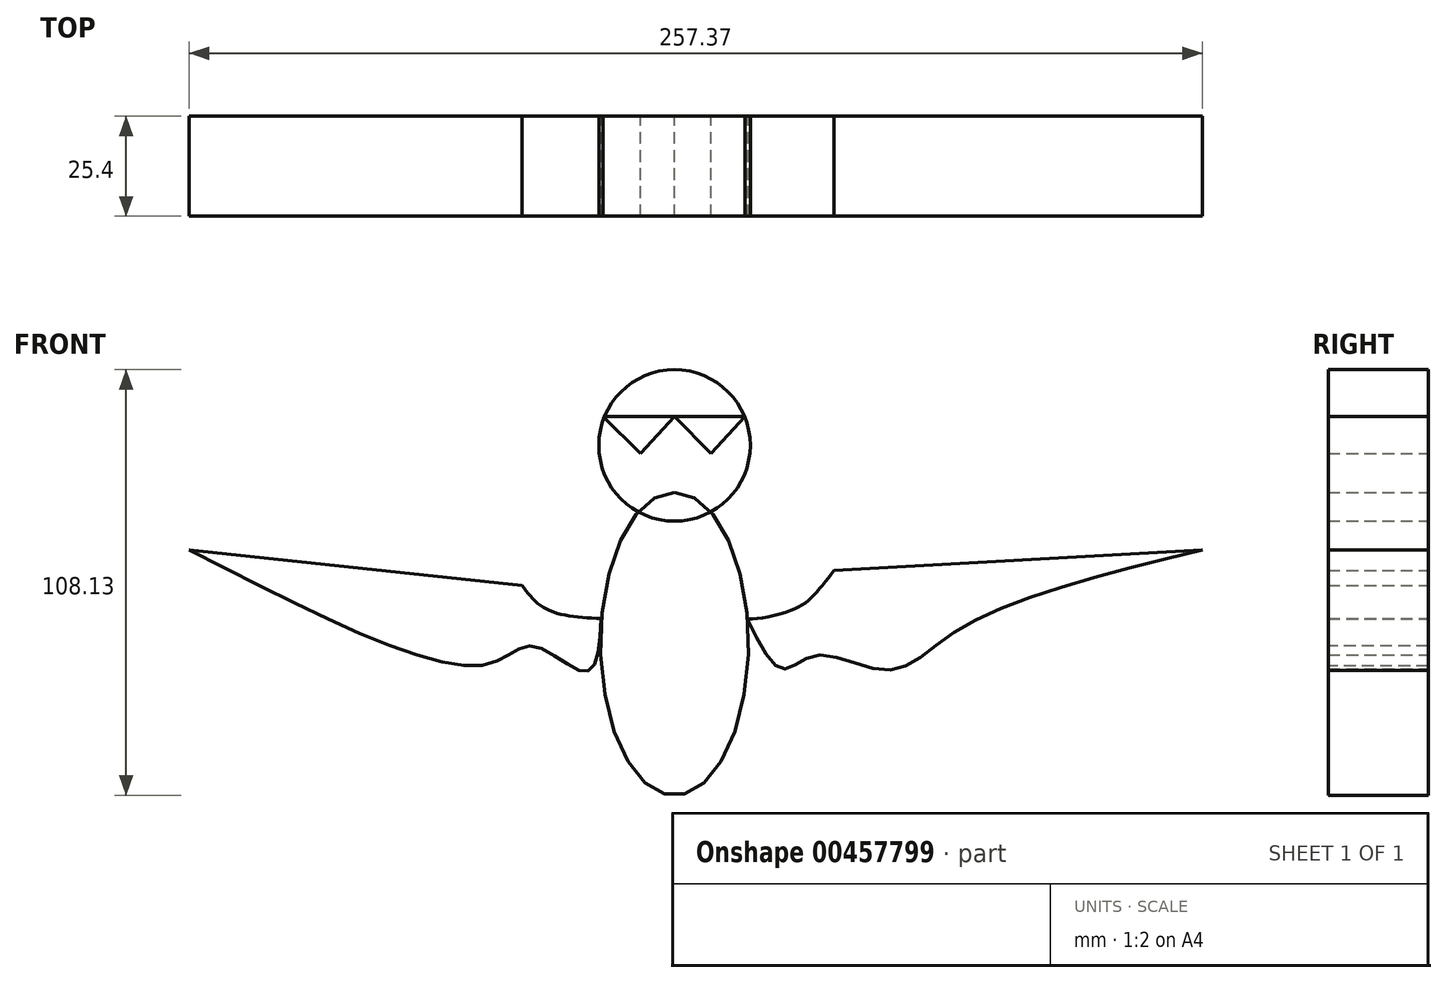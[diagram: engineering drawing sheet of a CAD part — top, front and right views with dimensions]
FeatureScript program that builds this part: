
annotation { "Feature Type Name" : "Feature", "Feature Type Description" : "" }
export const myFeature = defineFeature(function(context is Context, id is Id, definition is map)
    precondition{}
    {
        {
            var Q0;
            Q0=qCreatedBy(makeId("Front.planeOp"),FACE);
            var sketch = newSketch(context, id + "F0", { "sketchPlane" : qUnion([Q0])});
            skEllipse(sketch, "E0", {"center": v(0, -3.64) * mm, "majorRadius": 38.47 * mm, "minorRadius": 18.8 * mm, "majorAxis": v(0, 1)});
            skSolve(sketch);
        }
        {
            var Q0;
            Q0=qCreatedBy(makeId("Front.planeOp"),FACE);
            var sketch = newSketch(context, id + "F1", { "sketchPlane" : qUnion([Q0])});
            skFitSpline(sketch, "E1", {"points": [v(18.07, 8.3) * mm, v(25.36, 9.47) * mm, v(29.73, 20.26) * mm, v(31.48, 21.13) * mm, v(31.48, 20.55) * mm], "startDerivative": vector(25.4, -3.63) * mm, "endDerivative": vector(-2.02, -7.65) * mm});
            skLineSegment(sketch, "E2", {"start": v(31.54, 20.78) * mm, "end": v(134.08, 20.26) * mm});
            skLineSegment(sketch, "E3", {"start": v(134.08, 20.26) * mm, "end": v(40.52, 15.01) * mm});
            skFitSpline(sketch, "E4", {"points": [v(40.52, 15.01) * mm, v(34.98, 8.3) * mm, v(28.56, 4.52) * mm, v(18.36, 2.77) * mm, v(18.07, 3.35) * mm], "startDerivative": vector(-18.3, -24.2) * mm, "endDerivative": vector(-0.2, 8.2) * mm});
            skLineSegment(sketch, "E5", {"start": v(18.07, 8.3) * mm, "end": v(18.08, 3.12) * mm});
            skFitSpline(sketch, "E6", {"points": [v(18.36, 2.77) * mm, v(27.7, -10.06) * mm, v(35.85, -6.56) * mm, v(54.21, -10.35) * mm, v(72.29, 0) * mm, v(134.08, 20.26) * mm], "startDerivative": vector(55.94, -113.08) * mm, "endDerivative": vector(214.67, 52.98) * mm});
            skFitSpline(sketch, "E7", {"points": [v(-17.78, 8.3) * mm, v(-25.94, 8.3) * mm, v(-32.65, 19.67) * mm, v(-33.81, 20.26) * mm], "startDerivative": vector(-23.11, -7.76) * mm, "endDerivative": vector(-7.24, 0.33) * mm});
            skLineSegment(sketch, "E8", {"start": v(-33.81, 20.26) * mm, "end": v(-123.3, 20.26) * mm});
            skLineSegment(sketch, "E9", {"start": v(-123.3, 20.26) * mm, "end": v(-38.77, 11.22) * mm});
            skFitSpline(sketch, "E10", {"points": [v(-38.77, 11.22) * mm, v(-32.35, 5.1) * mm, v(-18.65, 2.77) * mm], "startDerivative": vector(12.18, -15.91) * mm, "endDerivative": vector(27.48, -1.53) * mm});
            skFitSpline(sketch, "E11", {"points": [v(-18.65, 2.77) * mm, v(-22.44, -10.64) * mm, v(-35.85, -4.23) * mm, v(-47.8, -8.9) * mm, v(-123.3, 20.26) * mm], "startDerivative": vector(-6.13, -105.57) * mm, "endDerivative": vector(-208.55, 107.64) * mm});
            skSolve(sketch);
        }
        {
            var Q0;
            Q0=qCreatedBy(makeId("Front.planeOp"),FACE);
            var sketch = newSketch(context, id + "F2", { "sketchPlane" : qUnion([Q0])});
            skFitSpline(sketch, "E12", {"points": [v(-10.1, -36.7) * mm, v(-24.14, -47.71) * mm, v(-22.71, -51.45) * mm, v(-17.74, -50.2) * mm, v(-22.36, -56.6) * mm, v(-20.76, -59.27) * mm, v(-11.16, -52.51) * mm, v(-6.36, -62.3) * mm, v(-4.05, -59.45) * mm, v(-8.31, -48.42) * mm, v(-5.3, -40.07) * mm], "startDerivative": vector(-127.16, -73.02) * mm, "endDerivative": vector(50.63, 74.74) * mm});
            skFitSpline(sketch, "E13", {"points": [v(9.11, -37.22) * mm, v(8.22, -43.98) * mm, v(8.93, -59.63) * mm, v(13.56, -59.98) * mm, v(13.56, -55.18) * mm, v(26.53, -59.63) * mm, v(27.25, -54.65) * mm, v(22.45, -54.3) * mm, v(25.82, -49.31) * mm, v(21.56, -47.36) * mm, v(16.4, -44.7) * mm, v(11.24, -34.02) * mm], "startDerivative": vector(-7.34, -61.02) * mm, "endDerivative": vector(-40.78, 108.1) * mm});
            skSolve(sketch);
        }
        {
            var Q0;
            Q0=qCreatedBy(makeId("Front.planeOp"),FACE);
            var sketch = newSketch(context, id + "F3", { "sketchPlane" : qUnion([Q0])});
            skFitSpline(sketch, "E14", {"points": [v(-18.25, 8.13) * mm, v(-20.7, -29.1) * mm, v(-16.14, -23.13) * mm], "startDerivative": vector(-9.88, -79.23) * mm, "endDerivative": vector(17.58, 30.62) * mm});
            skFitSpline(sketch, "E15", {"points": [v(18.29, 8.49) * mm, v(21.8, -23.13) * mm, v(22.86, -29.8) * mm, v(16.18, -23.13) * mm], "startDerivative": vector(5.55, -71.26) * mm, "endDerivative": vector(-32.66, 38.12) * mm});
            skSolve(sketch);
        }
        {
            var Q0;
            Q0=qCreatedBy(makeId("Front.planeOp"),FACE);
            var sketch = newSketch(context, id + "F4", { "sketchPlane" : qUnion([Q0])});
            skCircle(sketch, "E16", {"center": v(0, 46.77) * mm, "radius": 19.24 * mm});
            skSolve(sketch);
        }
        {
            var Q0;
            Q0=qCreatedBy(makeId("Front.planeOp"),FACE);
            var sketch = newSketch(context, id + "F5", { "sketchPlane" : qUnion([Q0])});
            skLineSegment(sketch, "E17", {"start": v(-18.22, 54.07) * mm, "end": v(0, 54.07) * mm});
            skLineSegment(sketch, "E18", {"start": v(0, 54.07) * mm, "end": v(-8.6, 44.74) * mm});
            skLineSegment(sketch, "E19", {"start": v(-8.6, 44.74) * mm, "end": v(-18.22, 54.07) * mm});
            skLineSegment(sketch, "E20", {"start": v(0, 54.07) * mm, "end": v(17.93, 54.07) * mm});
            skLineSegment(sketch, "E21", {"start": v(17.93, 54.07) * mm, "end": v(9.33, 44.74) * mm});
            skLineSegment(sketch, "E22", {"start": v(9.33, 44.74) * mm, "end": v(0, 54.07) * mm});
            skLineSegment(sketch, "E23", {"start": v(-8.6, 37.45) * mm, "end": v(0, 29.53) * mm});
            skLineSegment(sketch, "E24", {"start": v(0, 29.53) * mm, "end": v(7.7, 37.46) * mm});
            skSolve(sketch);
        }
        {
            var Q0;
            Q0=makeQuery(id+"F0.imprint","IMPRINT",FACE,{"disambiguationData":[TD([[makeQuery(id+"F0.imprint","IMPRINT",EDGE,{"derivedFrom":sQuery(id+"F0.wireOp",EDGE,"E0")}),1.0]])]});
            var Q1;
            {var subQ0=sQuery(id+"F1.wireOp",EDGE,"E3");Q1=makeQuery(id+"F1.imprint","IMPRINT",FACE,{"disambiguationData":[TD([[makeQuery(id+"F1.imprint","IMPRINT",EDGE,{"derivedFrom":subQ0}),1.0]])]});}
            var Q2;
            Q2=makeQuery(id+"F1.imprint","IMPRINT",FACE,{"disambiguationData":[TD([[makeQuery(id+"F1.imprint","IMPRINT",EDGE,{"derivedFrom":sQuery(id+"F1.wireOp",EDGE,"E9")}),-1.0]])]});
            var Q3;
            Q3=makeQuery(id+"F4.imprint","IMPRINT",FACE,{"disambiguationData":[TD([[makeQuery(id+"F4.imprint","IMPRINT",EDGE,{"derivedFrom":sQuery(id+"F4.wireOp",EDGE,"E16")}),1.0]])]});
            var Q4;
            Q4=makeQuery(id+"F5.imprint","IMPRINT",FACE,{"disambiguationData":[TD([[makeQuery(id+"F5.imprint","IMPRINT",EDGE,{"derivedFrom":sQuery(id+"F5.wireOp",EDGE,"E17")}),-1.0]])]});
            var Q5;
            Q5=makeQuery(id+"F5.imprint","IMPRINT",FACE,{"disambiguationData":[TD([[makeQuery(id+"F5.imprint","IMPRINT",EDGE,{"derivedFrom":sQuery(id+"F5.wireOp",EDGE,"E20")}),-1.0]])]});
            extrude(context, id + "F6", {"entities" : qUnion([Q0, Q1, Q2, Q3, Q4, Q5]), "depth" : 25.4 * mm});
        }
        {
            var Q0;
            Q0=sQuery(id+"F3.wireOp",EDGE,"E14");
            extrude(context, id + "F7", {"bodyType" : ToolBodyType.SURFACE, "surfaceEntities" : qUnion([Q0]), "depth" : 25.4 * mm});
        }
        {
            var Q0;
            Q0=qCreatedBy(makeId("Front.planeOp"),FACE);
            var sketch = newSketch(context, id + "F8", { "sketchPlane" : qUnion([Q0])});
            skFitSpline(sketch, "E25", {"points": [v(18.5, 0) * mm, v(20.55, -29.3) * mm, v(16.18, -24.63) * mm], "startDerivative": vector(8.7, -62.6) * mm, "endDerivative": vector(-16.4, 23.82) * mm});
            skSolve(sketch);
        }
        {
            var Q0;
            Q0=sQuery(id+"F8.wireOp",EDGE,"E25");
            extrude(context, id + "F9", {"bodyType" : ToolBodyType.SURFACE, "surfaceEntities" : qUnion([Q0]), "depth" : 25.4 * mm});
        }
        {
            var Q0;
            Q0=sQuery(id+"F2.wireOp",EDGE,"E12");
            extrude(context, id + "F10", {"bodyType" : ToolBodyType.SURFACE, "surfaceEntities" : qUnion([Q0]), "depth" : 25.4 * mm});
        }
        {
            var Q0;
            Q0=qCreatedBy(makeId("Front.planeOp"),FACE);
            var sketch = newSketch(context, id + "F11", { "sketchPlane" : qUnion([Q0])});
            skFitSpline(sketch, "E26", {"points": [v(11.8, -34.25) * mm, v(25.5, -47.36) * mm, v(15.01, -47.07) * mm, v(22, -55.53) * mm, v(10.06, -50.28) * mm, v(9.47, -62.52) * mm, v(3.35, -52.61) * mm, v(10.06, -42.7) * mm, v(8.02, -38.91) * mm], "startDerivative": vector(152.35, -115.6) * mm, "endDerivative": vector(-49.37, 46.76) * mm});
            skSolve(sketch);
        }
        {
            var Q0;
            Q0=sQuery(id+"F11.wireOp",EDGE,"E26");
            extrude(context, id + "F12", {"bodyType" : ToolBodyType.SURFACE, "surfaceEntities" : qUnion([Q0]), "depth" : 25.4 * mm});
        }
    });
